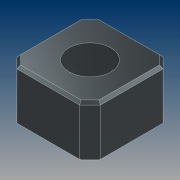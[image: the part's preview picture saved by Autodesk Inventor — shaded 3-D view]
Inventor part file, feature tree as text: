
AUTODESK INVENTOR PART (.ipt)
format: ipt  version: 2021 (Build 250183000, 183)  size: 111,616 bytes
history: native  units: mm
features: chamfer x2, extrude x1, sketch x1
ambient origin geometry x8: Origin, YZ Plane, XZ Plane, XY Plane, X Axis, Y Axis, Z Axis, Center Point
bodies: Solid1 (feature_tree)
feature tree (4):
  extrude  "Extrusion1"  Depth=10.0mm
  chamfer  "Chamfer1"  Distance=10.0mm
  chamfer  "Chamfer2"  Distance=2.0mm Angle=45.0deg
  sketch  "Sketch1"  dims[d0=16.0mm d1=8.0mm d2=10.0mm d3=0.0mm d4=2.0mm d5=2.0mm d6=45.0deg d7=0.5mm d8=2.0mm d9=45.0deg]
